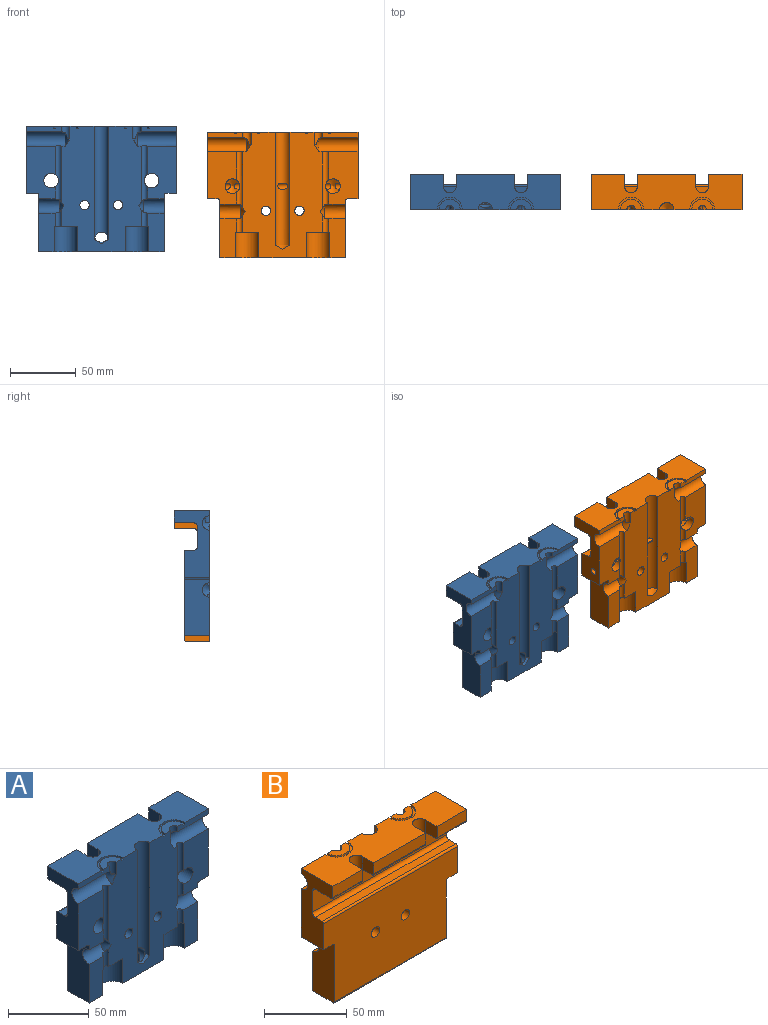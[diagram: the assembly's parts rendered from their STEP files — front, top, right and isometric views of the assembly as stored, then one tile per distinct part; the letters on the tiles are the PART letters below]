
ASSEMBLY  parts=2 mates=1
PART A: 290 faces, bbox 114.3x27x95.3 mm
  f0: plane 114.3x62.55mm, normal (0,1,0), area 5860.2mm2, adj f8,f29,f30,f37,f38,f39,f40,f41
  f1: plane 114.3x15.56mm, normal (0,1,0), area 1721.2mm2, adj f8,f32,f33,f37,f74,f75,f76,f77
  f2: plane 29.36x12.55mm, normal (0,-1,0), area 353.2mm2, adj f5,f21,f43,f60,f61,f73
  f3: plane 39.68x22.07mm, normal (0,-1,0), area 757.8mm2, adj f6,f8,f43,f44,f45,f64,f70,f73
  f4: plane 95.25x60.66mm, normal (0,-1,0), area 4067.1mm2, adj f5,f6,f9,f10,f11,f12,f16,f17
  f5: cylinder r=2.37mm len=12.68mm, axis (0,0,-1), area 83.3mm2, adj f2,f4,f61,f72,f73
  f6: cylinder r=2.37mm len=42.57mm, axis (0,0,-1), area 275.6mm2, adj f3,f4,f64,f70,f72,f73
  f7: plane 26.99x3.96mm, normal (0,-1,0), area 104.9mm2, adj f8,f9,f22,f23,f52,f53,f54,f70
  f8: plane 50.8x26.99mm, normal (1,0,0), area 800.2mm2, adj f0,f1,f3,f7,f22,f25,f30,f31
  f9: cylinder r=3.17mm len=9.53mm, axis (0,0,1), area 66.9mm2, adj f4,f7,f10,f23,f70,f71
  f10: plane 2.91x1.9mm, normal (0,0,1), area 1.4mm2, adj f4,f9,f71
  f11: cylinder r=2.37mm len=12.68mm, axis (0,0,-1), area 83.3mm2, adj f4,f14,f59,f68,f69
  f12: cylinder r=2.37mm len=42.57mm, axis (0,0,-1), area 275.5mm2, adj f4,f13,f65,f66,f68,f69
  f13: plane 39.68x22.07mm, normal (0,-1,0), area 757.8mm2, adj f12,f37,f38,f39,f40,f65,f66,f68
  f14: plane 29.36x12.55mm, normal (0,-1,0), area 353.2mm2, adj f11,f21,f38,f58,f59,f68
  f15: plane 26.99x3.96mm, normal (0,-1,0), area 104.9mm2, adj f16,f22,f28,f37,f55,f56,f57,f66
  f16: cylinder r=3.17mm len=9.53mm, axis (0,0,1), area 66.9mm2, adj f4,f15,f17,f28,f66,f67
  f17: plane 2.91x1.9mm, normal (0,0,1), area 1.4mm2, adj f4,f16,f67
  f18: cylinder r=5.56mm len=85.73mm, axis (0,0,1), area 1450mm2, adj f4,f19,f22,f62,f63
  f19: cone r=0mm half-angle=59deg, axis (0,0,1), area 29mm2, adj f4,f18,f63
  f20: cylinder r=5.08mm len=10.16mm, axis (0,0,-1), area 173.5mm2, adj f21,f62
  f21: plane 95.25x17.78mm, normal (0,0,-1), area 1364.2mm2, adj f2,f4,f14,f20,f29,f38,f43,f58
  f22: plane 114.3x26.99mm, normal (0,0,1), area 2498.3mm2, adj f4,f7,f8,f15,f18,f24,f25,f36
  f23: plane 15.88x7.94mm, normal (0,0,1), area 83.1mm2, adj f4,f7,f9,f53
  f24: plane 44.45x8.26mm, normal (0,1,0), area 366.9mm2, adj f22,f27,f46,f51
  f25: plane 25.4x8.26mm, normal (0,1,0), area 209.7mm2, adj f8,f22,f35,f48
  f26: cylinder r=1.27mm len=25.4mm, axis (-1,0,0), area 50.7mm2, adj f34,f36,f37,f49
  f27: cylinder r=1.27mm len=44.45mm, axis (-1,0,0), area 88.7mm2, adj f24,f34,f46,f51
  f28: plane 15.88x7.94mm, normal (0,0,1), area 83.1mm2, adj f4,f15,f16,f56
  f29: cylinder r=1.27mm len=95.25mm, axis (-1,0,0), area 190mm2, adj f0,f21,f38,f43
  f30: cylinder r=1.27mm len=114.3mm, axis (-1,0,0), area 228mm2, adj f0,f8,f31,f37
  f31: plane 114.3x5.72mm, normal (0,0,1), area 653.2mm2, adj f8,f30,f32,f37
  f32: cylinder r=2.54mm len=114.3mm, axis (-1,0,0), area 456mm2, adj f1,f8,f31,f37
  f33: cylinder r=2.54mm len=114.3mm, axis (-1,0,0), area 456mm2, adj f1,f8,f34,f37
  f34: plane 114.3x13.65mm, normal (0,0,-1), area 1332mm2, adj f8,f26,f27,f33,f35,f37,f46,f47
  f35: cylinder r=1.27mm len=25.4mm, axis (-1,0,0), area 50.7mm2, adj f8,f25,f34,f48
  f36: plane 25.4x8.26mm, normal (0,1,0), area 209.7mm2, adj f22,f26,f37,f49
  f37: plane 50.8x26.99mm, normal (-1,0,0), area 800.2mm2, adj f0,f1,f13,f15,f22,f26,f30,f31
  f38: plane 43.18x19.05mm, normal (-1,0,0), area 773.6mm2, adj f0,f13,f14,f21,f29,f40,f68
  f39: plane 19.05x8.26mm, normal (0,0,-1), area 157.3mm2, adj f0,f13,f37,f40
  f40: cylinder r=1.27mm len=19.05mm, axis (0,-1,0), area 38mm2, adj f0,f13,f38,f39
  f41: cylinder r=3.56mm len=19.05mm, axis (0,-1,0), area 425.6mm2, adj f0,f4
  f42: cylinder r=3.56mm len=19.05mm, axis (0,-1,0), area 425.6mm2, adj f0,f4
  f43: plane 43.18x19.05mm, normal (1,0,0), area 773.6mm2, adj f0,f2,f3,f21,f29,f45,f73
  f44: plane 19.05x8.26mm, normal (0,0,-1), area 157.3mm2, adj f0,f3,f8,f45
  f45: cylinder r=1.27mm len=19.05mm, axis (0,-1,0), area 38mm2, adj f0,f3,f43,f44
  f46: plane 9.53x9.53mm, normal (1,0,0), area 90.4mm2, adj f22,f24,f27,f34,f47
  f47: cylinder r=4.76mm len=9.53mm, axis (0,0,1), area 142.5mm2, adj f22,f34,f46,f48
  f48: plane 9.53x9.53mm, normal (-1,0,0), area 90.4mm2, adj f22,f25,f34,f35,f47
  f49: plane 9.53x9.53mm, normal (1,0,0), area 90.4mm2, adj f22,f26,f34,f36,f50
  f50: cylinder r=4.76mm len=9.53mm, axis (0,0,1), area 142.5mm2, adj f22,f34,f49,f51
  f51: plane 9.53x9.53mm, normal (-1,0,0), area 90.4mm2, adj f22,f24,f27,f34,f50
  f52: cylinder r=9.53mm len=19.05mm, axis (0,0,1), area 38mm2, adj f4,f7,f22,f54
  f53: cylinder r=7.94mm len=15.88mm, axis (0,0,1), area 31.7mm2, adj f4,f7,f23,f54
  f54: plane 19.05x9.53mm, normal (0,0,1), area 43.5mm2, adj f4,f7,f52,f53
  f55: cylinder r=9.53mm len=19.05mm, axis (0,0,1), area 38mm2, adj f4,f15,f22,f57
  f56: cylinder r=7.94mm len=15.88mm, axis (0,0,1), area 31.7mm2, adj f4,f15,f28,f57
  f57: plane 19.05x9.53mm, normal (0,0,1), area 43.5mm2, adj f4,f15,f55,f56
  f58: cylinder r=8.89mm len=19.05mm, axis (0,0,-1), area 532mm2, adj f4,f14,f21,f59
  f59: plane 17.78x8.89mm, normal (0,0,-1), area 115.3mm2, adj f4,f11,f14,f58
  f60: cylinder r=8.89mm len=19.05mm, axis (0,0,-1), area 532mm2, adj f2,f4,f21,f61
  f61: plane 17.78x8.89mm, normal (0,0,-1), area 115.3mm2, adj f2,f4,f5,f60
  f62: cylinder r=5.56mm len=15.24mm, axis (0,1,0), area 427.5mm2, adj f0,f18,f20,f63
  f63: cone r=0mm half-angle=59deg, axis (0,1,0), area 48.4mm2, adj f18,f19,f62
  f64: cylinder r=5.56mm len=19.05mm, axis (0,1,0), area 642.7mm2, adj f0,f3,f6
  f65: cylinder r=5.56mm len=19.05mm, axis (0,1,0), area 642.7mm2, adj f0,f12,f13
  f66: cylinder r=5.56mm len=29.85mm, axis (-1,0,0), area 505.3mm2, adj f4,f12,f13,f15,f16,f37,f67
  f67: cone r=0mm half-angle=59deg, axis (-1,0,0), area 37.8mm2, adj f4,f16,f17,f66
  f68: cylinder r=5.56mm len=15.88mm, axis (-1,0,0), area 263.8mm2, adj f11,f12,f13,f14,f38,f69
  f69: cone r=0mm half-angle=59deg, axis (-1,0,0), area 47.8mm2, adj f4,f11,f12,f68
  f70: cylinder r=5.56mm len=29.85mm, axis (1,0,0), area 505.3mm2, adj f3,f4,f6,f7,f8,f9,f71
  f71: cone r=0mm half-angle=59deg, axis (1,0,0), area 37.8mm2, adj f4,f9,f10,f70
  f72: cone r=0mm half-angle=59deg, axis (1,0,0), area 47.8mm2, adj f4,f5,f6,f73
  f73: cylinder r=5.56mm len=15.88mm, axis (1,0,0), area 263.8mm2, adj f2,f3,f5,f6,f43,f72
  f74: plane 1.27x0.59mm, normal (0,0,1), area 0.7mm2, adj f1,f75,f77,f78
  f75: plane 5.04x1.27mm, normal (1,0,0), area 6.4mm2, adj f1,f74,f76,f78
  f76: plane 1.27x0.59mm, normal (0,0,-1), area 0.7mm2, adj f1,f75,f77,f78
  f77: plane 5.04x1.27mm, normal (-1,0,0), area 6.4mm2, adj f1,f74,f76,f78
  f78: plane 5.04x0.59mm, normal (0,1,0), area 2.9mm2, adj f74,f75,f76,f77
  f79: extruded ~1.9x1.27mm, area 2.6mm2, adj f1,f80,f94,f95
  f80: extruded ~1.7x1.27mm, area 2.4mm2, adj f1,f79,f81,f95
  f81: extruded ~1.72x1.27mm, area 2.4mm2, adj f1,f80,f82,f95
  f82: extruded ~1.91x1.27mm, area 2.6mm2, adj f1,f81,f83,f95
  f83: extruded ~1.92x1.27mm, area 2.6mm2, adj f1,f82,f84,f95
  f84: extruded ~1.72x1.27mm, area 2.4mm2, adj f1,f83,f85,f95
  f85: extruded ~1.7x1.27mm, area 2.4mm2, adj f1,f84,f94,f95
  f86: extruded ~1.54x1.27mm, area 2.1mm2, adj f87,f93,f95,f96
  f87: extruded ~1.27x1.27mm, area 1.8mm2, adj f86,f88,f95,f96
  f88: extruded ~1.27x1.26mm, area 1.8mm2, adj f87,f89,f95,f96
  f89: extruded ~1.54x1.27mm, area 2.1mm2, adj f88,f90,f95,f96
  f90: extruded ~1.55x1.27mm, area 2.1mm2, adj f89,f91,f95,f96
  f91: extruded ~1.27x1.26mm, area 1.8mm2, adj f90,f92,f95,f96
  f92: extruded ~1.27x1.27mm, area 1.8mm2, adj f91,f93,f95,f96
  f93: extruded ~1.55x1.27mm, area 2.1mm2, adj f86,f92,f95,f96
  f94: extruded ~1.9x1.27mm, area 2.6mm2, adj f1,f79,f85,f95
  f95: plane 5.19x4.63mm, normal (0,1,0), area 8mm2, adj f79,f80,f81,f82,f83,f84,f85,f86
  f96: plane 4.15x3.39mm, normal (0,1,0), area 11.7mm2, adj f86,f87,f88,f89,f90,f91,f92,f93
  f97: extruded ~1.27x0.84mm, area 1.2mm2, adj f1,f98,f121,f122
  f98: extruded ~1.27x1.09mm, area 1.6mm2, adj f1,f97,f99,f122
  f99: extruded ~1.27x0.7mm, area 1mm2, adj f1,f98,f100,f122
  f100: extruded ~1.27x0.33mm, area 0.6mm2, adj f1,f99,f101,f122
  f101: extruded ~1.27x0.43mm, area 0.6mm2, adj f1,f100,f102,f122
  f102: extruded ~1.27x0.55mm, area 0.8mm2, adj f1,f101,f103,f122
  f103: extruded ~1.27x0.73mm, area 1mm2, adj f1,f102,f104,f122
  f104: extruded ~1.27x1.21mm, area 1.6mm2, adj f1,f103,f105,f122
  f105: plane 1.27x0.51mm, normal (0.94,0,0.34), area 0.7mm2, adj f1,f104,f106,f122
  f106: extruded ~1.38x1.27mm, area 1.8mm2, adj f1,f105,f107,f122
  f107: extruded ~1.27x1.16mm, area 1.6mm2, adj f1,f106,f108,f122
  f108: extruded ~1.27x0.93mm, area 1.4mm2, adj f1,f107,f109,f122
  f109: extruded ~1.27x0.9mm, area 1.2mm2, adj f1,f108,f110,f122
  f110: extruded ~1.27x1mm, area 1.5mm2, adj f1,f109,f111,f122
  f111: extruded ~1.27x0.75mm, area 1mm2, adj f1,f110,f112,f122
  f112: extruded ~1.27x0.35mm, area 0.6mm2, adj f1,f111,f113,f122
  f113: extruded ~1.27x0.43mm, area 0.6mm2, adj f1,f112,f114,f122
  f114: extruded ~1.27x0.62mm, area 0.9mm2, adj f1,f113,f115,f122
  f115: extruded ~1.27x0.88mm, area 1.2mm2, adj f1,f114,f116,f122
  f116: extruded ~1.27x0.72mm, area 0.9mm2, adj f1,f115,f117,f122
  f117: extruded ~1.27x0.68mm, area 0.9mm2, adj f1,f116,f118,f122
  f118: plane 1.27x0.56mm, normal (-1,0,0), area 0.7mm2, adj f1,f117,f119,f122
  f119: extruded ~1.38x1.27mm, area 1.8mm2, adj f1,f118,f120,f122
  f120: extruded ~1.31x1.27mm, area 1.8mm2, adj f1,f119,f121,f122
  f121: extruded ~1.27x1.04mm, area 1.5mm2, adj f1,f97,f120,f122
  f122: plane 5.18x3.17mm, normal (0,1,0), area 5.9mm2, adj f97,f98,f99,f100,f101,f102,f103,f104
  f123: plane 1.27x0.59mm, normal (0,0,1), area 0.7mm2, adj f1,f124,f126,f127
  f124: plane 5.04x1.27mm, normal (1,0,0), area 6.4mm2, adj f1,f123,f125,f127
  f125: plane 1.27x0.59mm, normal (0,0,-1), area 0.7mm2, adj f1,f124,f126,f127
  f126: plane 5.04x1.27mm, normal (-1,0,0), area 6.4mm2, adj f1,f123,f125,f127
  f127: plane 5.04x0.59mm, normal (0,1,0), area 2.9mm2, adj f123,f124,f125,f126
  f128: extruded ~1.27x0.84mm, area 1.2mm2, adj f1,f129,f152,f153
  f129: extruded ~1.27x1.09mm, area 1.6mm2, adj f1,f128,f130,f153
  f130: extruded ~1.27x0.7mm, area 1mm2, adj f1,f129,f131,f153
  f131: extruded ~1.27x0.33mm, area 0.6mm2, adj f1,f130,f132,f153
  f132: extruded ~1.27x0.43mm, area 0.6mm2, adj f1,f131,f133,f153
  f133: extruded ~1.27x0.55mm, area 0.8mm2, adj f1,f132,f134,f153
  f134: extruded ~1.27x0.73mm, area 1mm2, adj f1,f133,f135,f153
  f135: extruded ~1.27x1.21mm, area 1.6mm2, adj f1,f134,f136,f153
  f136: plane 1.27x0.51mm, normal (0.94,0,0.34), area 0.7mm2, adj f1,f135,f137,f153
  f137: extruded ~1.38x1.27mm, area 1.8mm2, adj f1,f136,f138,f153
  f138: extruded ~1.27x1.16mm, area 1.6mm2, adj f1,f137,f139,f153
  f139: extruded ~1.27x0.93mm, area 1.4mm2, adj f1,f138,f140,f153
  f140: extruded ~1.27x0.9mm, area 1.2mm2, adj f1,f139,f141,f153
  f141: extruded ~1.27x1mm, area 1.5mm2, adj f1,f140,f142,f153
  f142: extruded ~1.27x0.75mm, area 1mm2, adj f1,f141,f143,f153
  f143: extruded ~1.27x0.35mm, area 0.6mm2, adj f1,f142,f144,f153
  f144: extruded ~1.27x0.43mm, area 0.6mm2, adj f1,f143,f145,f153
  f145: extruded ~1.27x0.62mm, area 0.9mm2, adj f1,f144,f146,f153
  f146: extruded ~1.27x0.88mm, area 1.2mm2, adj f1,f145,f147,f153
  f147: extruded ~1.27x0.72mm, area 0.9mm2, adj f1,f146,f148,f153
  f148: extruded ~1.27x0.68mm, area 0.9mm2, adj f1,f147,f149,f153
  f149: plane 1.27x0.56mm, normal (-1,0,0), area 0.7mm2, adj f1,f148,f150,f153
  f150: extruded ~1.38x1.27mm, area 1.8mm2, adj f1,f149,f151,f153
  f151: extruded ~1.31x1.27mm, area 1.8mm2, adj f1,f150,f152,f153
  f152: extruded ~1.27x1.04mm, area 1.5mm2, adj f1,f128,f151,f153
  f153: plane 5.18x3.17mm, normal (0,1,0), area 5.9mm2, adj f128,f129,f130,f131,f132,f133,f134,f135
  f154: extruded ~1.9x1.27mm, area 2.6mm2, adj f1,f155,f169,f170
  f155: extruded ~1.7x1.27mm, area 2.4mm2, adj f1,f154,f156,f170
  f156: extruded ~1.72x1.27mm, area 2.4mm2, adj f1,f155,f157,f170
  f157: extruded ~1.91x1.27mm, area 2.6mm2, adj f1,f156,f158,f170
  f158: extruded ~1.92x1.27mm, area 2.6mm2, adj f1,f157,f159,f170
  f159: extruded ~1.72x1.27mm, area 2.4mm2, adj f1,f158,f160,f170
  f160: extruded ~1.7x1.27mm, area 2.4mm2, adj f1,f159,f169,f170
  f161: extruded ~1.54x1.27mm, area 2.1mm2, adj f162,f168,f170,f171
  f162: extruded ~1.27x1.27mm, area 1.8mm2, adj f161,f163,f170,f171
  f163: extruded ~1.27x1.26mm, area 1.8mm2, adj f162,f164,f170,f171
  f164: extruded ~1.54x1.27mm, area 2.1mm2, adj f163,f165,f170,f171
  f165: extruded ~1.55x1.27mm, area 2.1mm2, adj f164,f166,f170,f171
  f166: extruded ~1.27x1.26mm, area 1.8mm2, adj f165,f167,f170,f171
  f167: extruded ~1.27x1.27mm, area 1.8mm2, adj f166,f168,f170,f171
  f168: extruded ~1.55x1.27mm, area 2.1mm2, adj f161,f167,f170,f171
  f169: extruded ~1.9x1.27mm, area 2.6mm2, adj f1,f154,f160,f170
  f170: plane 5.19x4.63mm, normal (0,1,0), area 8mm2, adj f154,f155,f156,f157,f158,f159,f160,f161
  f171: plane 4.15x3.39mm, normal (0,1,0), area 11.7mm2, adj f161,f162,f163,f164,f165,f166,f167,f168
  f172: extruded ~1.9x1.27mm, area 2.6mm2, adj f0,f173,f191,f192
  f173: extruded ~1.7x1.27mm, area 2.4mm2, adj f0,f172,f174,f192
  f174: extruded ~1.72x1.27mm, area 2.4mm2, adj f0,f173,f175,f192
  f175: extruded ~1.91x1.27mm, area 2.6mm2, adj f0,f174,f176,f192
  f176: extruded ~1.92x1.27mm, area 2.6mm2, adj f0,f175,f177,f192
  f177: extruded ~1.72x1.27mm, area 2.4mm2, adj f0,f176,f178,f192
  f178: plane 1.27x0.19mm, normal (0.04,0,1), area 0.2mm2, adj f0,f177,f179,f192
  f179: plane 1.27x1.14mm, normal (-0.76,0,0.65), area 1.9mm2, adj f0,f178,f180,f192
  f180: plane 1.27x0.85mm, normal (0,0,1), area 1.1mm2, adj f0,f179,f181,f192
  f181: plane 1.27x1.25mm, normal (0.72,0,-0.69), area 2.2mm2, adj f0,f180,f182,f192
  f182: extruded ~1.27x1.1mm, area 1.8mm2, adj f0,f181,f191,f192
  f183: extruded ~1.54x1.27mm, area 2.1mm2, adj f184,f190,f192,f193
  f184: extruded ~1.27x1.27mm, area 1.8mm2, adj f183,f185,f192,f193
  f185: extruded ~1.27x1.26mm, area 1.8mm2, adj f184,f186,f192,f193
  f186: extruded ~1.54x1.27mm, area 2.1mm2, adj f185,f187,f192,f193
  f187: extruded ~1.55x1.27mm, area 2.1mm2, adj f186,f188,f192,f193
  f188: extruded ~1.27x1.26mm, area 1.8mm2, adj f187,f189,f192,f193
  f189: extruded ~1.27x1.27mm, area 1.8mm2, adj f188,f190,f192,f193
  f190: extruded ~1.55x1.27mm, area 2.1mm2, adj f183,f189,f192,f193
  f191: extruded ~1.61x1.27mm, area 2.1mm2, adj f0,f172,f182,f192
  f192: plane 6.32x4.63mm, normal (0,1,0), area 9mm2, adj f172,f173,f174,f175,f176,f177,f178,f179
  f193: plane 4.15x3.39mm, normal (0,1,0), area 11.7mm2, adj f183,f184,f185,f186,f187,f188,f189,f190
  f194: plane 1.27x0.52mm, normal (1,0,0), area 0.7mm2, adj f0,f195,f205,f206
  f195: plane 2.22x1.27mm, normal (0,0,-1), area 2.8mm2, adj f0,f194,f196,f206
  f196: plane 1.85x1.27mm, normal (1,0,0), area 2.4mm2, adj f0,f195,f197,f206
  f197: plane 2.09x1.27mm, normal (0,0,1), area 2.7mm2, adj f0,f196,f198,f206
  f198: plane 1.27x0.52mm, normal (1,0,0), area 0.7mm2, adj f0,f197,f199,f206
  f199: plane 2.09x1.27mm, normal (0,0,-1), area 2.7mm2, adj f0,f198,f200,f206
  f200: plane 1.62x1.27mm, normal (1,0,0), area 2.1mm2, adj f0,f199,f201,f206
  f201: plane 2.22x1.27mm, normal (0,0,1), area 2.8mm2, adj f0,f200,f202,f206
  f202: plane 1.27x0.52mm, normal (1,0,0), area 0.7mm2, adj f0,f201,f203,f206
  f203: plane 2.81x1.27mm, normal (0,0,-1), area 3.6mm2, adj f0,f202,f204,f206
  f204: plane 5.04x1.27mm, normal (-1,0,0), area 6.4mm2, adj f0,f203,f205,f206
  f205: plane 2.81x1.27mm, normal (0,0,1), area 3.6mm2, adj f0,f194,f204,f206
  f206: plane 5.04x2.81mm, normal (0,1,0), area 6.3mm2, adj f194,f195,f196,f197,f198,f199,f200,f201
  f207: plane 1.27x0.52mm, normal (1,0,0), area 0.7mm2, adj f0,f208,f218,f219
  f208: plane 2.22x1.27mm, normal (0,0,-1), area 2.8mm2, adj f0,f207,f209,f219
  f209: plane 1.85x1.27mm, normal (1,0,0), area 2.4mm2, adj f0,f208,f210,f219
  f210: plane 2.09x1.27mm, normal (0,0,1), area 2.7mm2, adj f0,f209,f211,f219
  f211: plane 1.27x0.52mm, normal (1,0,0), area 0.7mm2, adj f0,f210,f212,f219
  f212: plane 2.09x1.27mm, normal (0,0,-1), area 2.7mm2, adj f0,f211,f213,f219
  f213: plane 1.62x1.27mm, normal (1,0,0), area 2.1mm2, adj f0,f212,f214,f219
  f214: plane 2.22x1.27mm, normal (0,0,1), area 2.8mm2, adj f0,f213,f215,f219
  f215: plane 1.27x0.52mm, normal (1,0,0), area 0.7mm2, adj f0,f214,f216,f219
  f216: plane 2.81x1.27mm, normal (0,0,-1), area 3.6mm2, adj f0,f215,f217,f219
  f217: plane 5.04x1.27mm, normal (-1,0,0), area 6.4mm2, adj f0,f216,f218,f219
  f218: plane 2.81x1.27mm, normal (0,0,1), area 3.6mm2, adj f0,f207,f217,f219
  f219: plane 5.04x2.81mm, normal (0,1,0), area 6.3mm2, adj f207,f208,f209,f210,f211,f212,f213,f214
  f220: plane 4.15x1.27mm, normal (1,0,0), area 5.3mm2, adj f0,f221,f227,f228
  f221: plane 1.37x1.27mm, normal (0,0,1), area 1.7mm2, adj f0,f220,f222,f228
  f222: plane 1.27x0.89mm, normal (1,0,0), area 1.1mm2, adj f0,f221,f223,f228
  f223: plane 3.8x1.27mm, normal (0,0,-1), area 4.8mm2, adj f0,f222,f224,f228
  f224: plane 1.27x0.89mm, normal (-1,0,0), area 1.1mm2, adj f0,f223,f225,f228
  f225: plane 1.37x1.27mm, normal (0,0,1), area 1.7mm2, adj f0,f224,f226,f228
  f226: plane 4.15x1.27mm, normal (-1,0,0), area 5.3mm2, adj f0,f225,f227,f228
  f227: plane 1.27x1.07mm, normal (0,0,1), area 1.4mm2, adj f0,f220,f226,f228
  f228: plane 5.04x3.8mm, normal (0,1,0), area 7.8mm2, adj f220,f221,f222,f223,f224,f225,f226,f227
  f229: extruded ~1.9x1.27mm, area 2.6mm2, adj f0,f230,f248,f249
  f230: extruded ~1.7x1.27mm, area 2.4mm2, adj f0,f229,f231,f249
  f231: extruded ~1.72x1.27mm, area 2.4mm2, adj f0,f230,f232,f249
  f232: extruded ~1.91x1.27mm, area 2.6mm2, adj f0,f231,f233,f249
  f233: extruded ~1.92x1.27mm, area 2.6mm2, adj f0,f232,f234,f249
  f234: extruded ~1.72x1.27mm, area 2.4mm2, adj f0,f233,f235,f249
  f235: plane 1.27x0.19mm, normal (0.04,0,1), area 0.2mm2, adj f0,f234,f236,f249
  f236: plane 1.27x1.14mm, normal (-0.76,0,0.65), area 1.9mm2, adj f0,f235,f237,f249
  f237: plane 1.27x0.85mm, normal (0,0,1), area 1.1mm2, adj f0,f236,f238,f249
  f238: plane 1.27x1.25mm, normal (0.72,0,-0.69), area 2.2mm2, adj f0,f237,f239,f249
  f239: extruded ~1.27x1.1mm, area 1.8mm2, adj f0,f238,f248,f249
  f240: extruded ~1.54x1.27mm, area 2.1mm2, adj f241,f247,f249,f250
  f241: extruded ~1.27x1.27mm, area 1.8mm2, adj f240,f242,f249,f250
  f242: extruded ~1.27x1.26mm, area 1.8mm2, adj f241,f243,f249,f250
  f243: extruded ~1.54x1.27mm, area 2.1mm2, adj f242,f244,f249,f250
  f244: extruded ~1.55x1.27mm, area 2.1mm2, adj f243,f245,f249,f250
  f245: extruded ~1.27x1.26mm, area 1.8mm2, adj f244,f246,f249,f250
  f246: extruded ~1.27x1.27mm, area 1.8mm2, adj f245,f247,f249,f250
  f247: extruded ~1.55x1.27mm, area 2.1mm2, adj f240,f246,f249,f250
  f248: extruded ~1.61x1.27mm, area 2.1mm2, adj f0,f229,f239,f249
  f249: plane 6.32x4.63mm, normal (0,1,0), area 9mm2, adj f229,f230,f231,f232,f233,f234,f235,f236
  f250: plane 4.15x3.39mm, normal (0,1,0), area 11.7mm2, adj f240,f241,f242,f243,f244,f245,f246,f247
  f251: plane 3x1.27mm, normal (-0.95,0,-0.3), area 4mm2, adj f0,f252,f260,f261
  f252: extruded ~1.27x1.11mm, area 1.4mm2, adj f0,f251,f253,f261
  f253: extruded ~1.27x0.49mm, area 0.6mm2, adj f0,f252,f254,f261
  f254: extruded ~1.27x0.62mm, area 0.8mm2, adj f0,f253,f255,f261
  f255: plane 3x1.27mm, normal (0.95,0,-0.3), area 4mm2, adj f0,f254,f256,f261
  f256: plane 1.27x1.08mm, normal (0,0,-1), area 1.4mm2, adj f0,f255,f257,f261
  f257: plane 5.04x1.71mm, normal (-0.95,0,0.32), area 6.8mm2, adj f0,f256,f258,f261
  f258: plane 1.27x1.16mm, normal (0,0,1), area 1.5mm2, adj f0,f257,f259,f261
  f259: plane 5.04x1.71mm, normal (0.95,0,0.32), area 6.8mm2, adj f0,f258,f260,f261
  f260: plane 1.27x1.08mm, normal (0,0,-1), area 1.4mm2, adj f0,f251,f259,f261
  f261: plane 5.04x4.59mm, normal (0,1,0), area 9.8mm2, adj f251,f252,f253,f254,f255,f256,f257,f258
  f262: plane 1.27x0.88mm, normal (1,0,0), area 1.1mm2, adj f0,f263,f273,f274
  f263: plane 1.83x1.27mm, normal (0,0,-1), area 2.3mm2, adj f0,f262,f264,f274
  f264: plane 1.3x1.27mm, normal (1,0,0), area 1.6mm2, adj f0,f263,f265,f274
  f265: plane 1.71x1.27mm, normal (0,0,1), area 2.2mm2, adj f0,f264,f266,f274
  f266: plane 1.27x0.88mm, normal (1,0,0), area 1.1mm2, adj f0,f265,f267,f274
  f267: plane 1.71x1.27mm, normal (0,0,-1), area 2.2mm2, adj f0,f266,f268,f274
  f268: plane 1.27x1.11mm, normal (1,0,0), area 1.4mm2, adj f0,f267,f269,f274
  f269: plane 1.83x1.27mm, normal (0,0,1), area 2.3mm2, adj f0,f268,f270,f274
  f270: plane 1.27x0.88mm, normal (1,0,0), area 1.1mm2, adj f0,f269,f271,f274
  f271: plane 2.9x1.27mm, normal (0,0,-1), area 3.7mm2, adj f0,f270,f272,f274
  f272: plane 5.04x1.27mm, normal (-1,0,0), area 6.4mm2, adj f0,f271,f273,f274
  f273: plane 2.9x1.27mm, normal (0,0,1), area 3.7mm2, adj f0,f262,f272,f274
  f274: plane 5.04x2.9mm, normal (0,1,0), area 10.1mm2, adj f262,f263,f264,f265,f266,f267,f268,f269
  f275: plane 5.04x1.27mm, normal (1,0,0), area 6.4mm2, adj f0,f276,f288,f289
  f276: plane 1.27x0.96mm, normal (0,0,-1), area 1.2mm2, adj f0,f275,f277,f289
  f277: plane 2.38x1.27mm, normal (-1,0,0), area 3mm2, adj f0,f276,f278,f289
  f278: extruded ~1.39x1.27mm, area 1.8mm2, adj f0,f277,f279,f289
  f279: plane 1.27x0.02mm, normal (0,0,-1), area 0mm2, adj f0,f278,f280,f289
  f280: plane 3.77x2.19mm, normal (0.87,0,-0.5), area 5.5mm2, adj f0,f279,f281,f289
  f281: plane 1.35x1.27mm, normal (0,0,-1), area 1.7mm2, adj f0,f280,f282,f289
  f282: plane 5.04x1.27mm, normal (-1,0,0), area 6.4mm2, adj f0,f281,f283,f289
  f283: plane 1.27x0.95mm, normal (0,0,1), area 1.2mm2, adj f0,f282,f284,f289
  f284: plane 2.37x1.27mm, normal (1,0,0), area 3mm2, adj f0,f283,f285,f289
  f285: extruded ~1.44x1.27mm, area 1.8mm2, adj f0,f284,f286,f289
  f286: plane 1.27x0.03mm, normal (0,0,1), area 0mm2, adj f0,f285,f287,f289
  f287: plane 3.81x2.19mm, normal (-0.87,0,0.5), area 5.6mm2, adj f0,f286,f288,f289
  f288: plane 1.36x1.27mm, normal (0,0,1), area 1.7mm2, adj f0,f275,f287,f289
  f289: plane 5.04x4.47mm, normal (0,1,0), area 14.4mm2, adj f275,f276,f277,f278,f279,f280,f281,f282
PART B: 77 faces, bbox 114.3x27x95.3 mm
  f0: cylinder r=5.56mm len=85.73mm, axis (0,0,1), area 1466.2mm2, adj f7,f24,f60,f75
  f1: cylinder r=5.56mm len=11.13mm, axis (0,1,0), area 180.7mm2, adj f2,f6,f8,f75,f76
  f2: cone r=0mm half-angle=59deg, axis (0,1,0), area 77.1mm2, adj f1,f75,f76
  f3: cylinder r=5.56mm len=11.13mm, axis (0,1,0), area 180.7mm2, adj f4,f14,f16,f74,f75
  f4: cone r=0mm half-angle=59deg, axis (0,1,0), area 77.1mm2, adj f3,f74,f75
  f5: plane 29.36x12.55mm, normal (0,1,0), area 353.2mm2, adj f9,f21,f45,f63,f64,f72
  f6: plane 39.68x22.07mm, normal (0,1,0), area 757.8mm2, adj f1,f8,f11,f45,f46,f47,f69,f72
  f7: plane 95.25x60.66mm, normal (0,1,0), area 4067.1mm2, adj f0,f8,f9,f12,f13,f14,f15,f19
  f8: cylinder r=2.37mm len=42.57mm, axis (0,0,-1), area 275.5mm2, adj f1,f6,f7,f69,f71,f72
  f9: cylinder r=2.37mm len=12.68mm, axis (0,0,-1), area 83.3mm2, adj f5,f7,f63,f71,f72
  f10: plane 26.99x3.96mm, normal (0,1,0), area 104.9mm2, adj f11,f13,f23,f24,f54,f55,f56,f69
  f11: plane 50.8x26.99mm, normal (1,0,0), area 782.5mm2, adj f6,f10,f24,f26,f28,f29,f31,f34
  f12: plane 2.91x1.9mm, normal (0,0,1), area 1.4mm2, adj f7,f13,f70
  f13: cylinder r=3.17mm len=9.53mm, axis (0,0,1), area 66.7mm2, adj f7,f10,f12,f23,f69,f70
  f14: cylinder r=2.37mm len=42.57mm, axis (0,0,-1), area 275.6mm2, adj f3,f7,f16,f65,f67,f68
  f15: cylinder r=2.37mm len=12.68mm, axis (0,0,-1), area 83.3mm2, adj f7,f17,f61,f67,f68
  f16: plane 39.68x22.07mm, normal (0,1,0), area 757.8mm2, adj f3,f14,f39,f40,f41,f42,f65,f67
  f17: plane 29.36x12.55mm, normal (0,1,0), area 353.2mm2, adj f15,f21,f40,f61,f62,f67
  f18: plane 26.99x3.96mm, normal (0,1,0), area 104.9mm2, adj f19,f22,f24,f39,f57,f58,f59,f65
  f19: cylinder r=3.17mm len=9.53mm, axis (0,0,1), area 66.7mm2, adj f7,f18,f20,f22,f65,f66
  f20: plane 2.91x1.9mm, normal (0,0,1), area 1.4mm2, adj f7,f19,f66
  f21: plane 95.25x17.78mm, normal (0,0,-1), area 1445.3mm2, adj f5,f7,f17,f30,f40,f45,f62,f64
  f22: plane 15.88x7.94mm, normal (0,0,1), area 83.1mm2, adj f7,f18,f19,f58
  f23: plane 15.88x7.94mm, normal (0,0,1), area 83.1mm2, adj f7,f10,f13,f55
  f24: plane 114.3x26.99mm, normal (0,0,1), area 2498.3mm2, adj f0,f7,f10,f11,f18,f25,f26,f32
  f25: plane 44.45x8.26mm, normal (0,-1,0), area 366.9mm2, adj f24,f27,f50,f52
  f26: plane 25.4x8.26mm, normal (0,-1,0), area 209.7mm2, adj f11,f24,f28,f48
  f27: cylinder r=1.27mm len=44.45mm, axis (-1,0,0), area 88.7mm2, adj f25,f29,f50,f52
  f28: cylinder r=1.27mm len=25.4mm, axis (-1,0,0), area 50.7mm2, adj f11,f26,f29,f48
  f29: plane 114.3x13.65mm, normal (0,0,-1), area 1332mm2, adj f11,f27,f28,f33,f34,f39,f48,f49
  f30: cylinder r=1.27mm len=95.25mm, axis (-1,0,0), area 190mm2, adj f21,f31,f40,f45
  f31: plane 114.3x62.55mm, normal (0,-1,0), area 6247.8mm2, adj f11,f30,f38,f39,f40,f41,f42,f43
  f32: plane 25.4x8.26mm, normal (0,-1,0), area 209.7mm2, adj f24,f33,f39,f53
  f33: cylinder r=1.27mm len=25.4mm, axis (-1,0,0), area 50.7mm2, adj f29,f32,f39,f53
  f34: cylinder r=2.54mm len=114.3mm, axis (-1,0,0), area 456mm2, adj f11,f29,f35,f39
  f35: plane 114.3x15.56mm, normal (0,-1,0), area 1778.2mm2, adj f11,f34,f36,f39
  f36: cylinder r=2.54mm len=114.3mm, axis (-1,0,0), area 456mm2, adj f11,f35,f37,f39
  f37: plane 114.3x5.72mm, normal (0,0,1), area 653.2mm2, adj f11,f36,f38,f39
  f38: cylinder r=1.27mm len=114.3mm, axis (-1,0,0), area 228mm2, adj f11,f31,f37,f39
  f39: plane 50.8x26.99mm, normal (-1,0,0), area 800.2mm2, adj f16,f18,f24,f29,f31,f32,f33,f34
  f40: plane 43.18x19.05mm, normal (-1,0,0), area 773.6mm2, adj f16,f17,f21,f30,f31,f41,f67
  f41: cylinder r=1.27mm len=19.05mm, axis (0,-1,0), area 38mm2, adj f16,f31,f40,f42
  f42: plane 19.05x8.26mm, normal (0,0,-1), area 157.3mm2, adj f16,f31,f39,f41
  f43: cylinder r=3.56mm len=19.05mm, axis (0,-1,0), area 425.6mm2, adj f7,f31
  f44: cylinder r=3.56mm len=19.05mm, axis (0,-1,0), area 425.6mm2, adj f7,f31
  f45: plane 43.18x19.05mm, normal (1,0,0), area 773.6mm2, adj f5,f6,f21,f30,f31,f46,f72
  f46: cylinder r=1.27mm len=19.05mm, axis (0,-1,0), area 38mm2, adj f6,f31,f45,f47
  f47: plane 19.05x8.26mm, normal (0,0,-1), area 157.3mm2, adj f6,f11,f31,f46
  f48: plane 9.53x9.53mm, normal (-1,0,0), area 90.4mm2, adj f24,f26,f28,f29,f49
  f49: cylinder r=4.76mm len=9.53mm, axis (0,0,1), area 142.5mm2, adj f24,f29,f48,f50
  f50: plane 9.53x9.53mm, normal (1,0,0), area 90.4mm2, adj f24,f25,f27,f29,f49
  f51: cylinder r=4.76mm len=9.53mm, axis (0,0,1), area 142.5mm2, adj f24,f29,f52,f53
  f52: plane 9.53x9.53mm, normal (-1,0,0), area 90.4mm2, adj f24,f25,f27,f29,f51
  f53: plane 9.53x9.53mm, normal (1,0,0), area 90.4mm2, adj f24,f29,f32,f33,f51
  f54: cylinder r=9.53mm len=19.05mm, axis (0,0,1), area 38mm2, adj f7,f10,f24,f56
  f55: cylinder r=7.94mm len=15.88mm, axis (0,0,1), area 31.7mm2, adj f7,f10,f23,f56
  f56: plane 19.05x9.53mm, normal (0,0,1), area 43.5mm2, adj f7,f10,f54,f55
  f57: cylinder r=9.53mm len=19.05mm, axis (0,0,1), area 38mm2, adj f7,f18,f24,f59
  f58: cylinder r=7.94mm len=15.88mm, axis (0,0,1), area 31.7mm2, adj f7,f18,f22,f59
  f59: plane 19.05x9.53mm, normal (0,0,1), area 43.5mm2, adj f7,f18,f57,f58
  f60: cone r=0mm half-angle=59deg, axis (0,0,1), area 56.7mm2, adj f0,f7
  f61: plane 17.78x8.89mm, normal (0,0,-1), area 115.3mm2, adj f7,f15,f17,f62
  f62: cylinder r=8.89mm len=19.05mm, axis (0,0,-1), area 532mm2, adj f7,f17,f21,f61
  f63: plane 17.78x8.89mm, normal (0,0,-1), area 115.3mm2, adj f5,f7,f9,f64
  f64: cylinder r=8.89mm len=19.05mm, axis (0,0,-1), area 532mm2, adj f5,f7,f21,f63
  f65: cylinder r=5.56mm len=29.85mm, axis (-1,0,0), area 505.3mm2, adj f7,f14,f16,f18,f19,f39,f66
  f66: cone r=0mm half-angle=59deg, axis (-1,0,0), area 37.8mm2, adj f7,f19,f20,f65
  f67: cylinder r=5.56mm len=15.88mm, axis (-1,0,0), area 263.8mm2, adj f14,f15,f16,f17,f40,f68
  f68: cone r=0mm half-angle=59deg, axis (-1,0,0), area 47.8mm2, adj f7,f14,f15,f67
  f69: cylinder r=5.56mm len=29.85mm, axis (1,0,0), area 505.3mm2, adj f6,f7,f8,f10,f11,f13,f70
  f70: cone r=0mm half-angle=59deg, axis (1,0,0), area 37.8mm2, adj f7,f12,f13,f69
  f71: cone r=0mm half-angle=59deg, axis (1,0,0), area 47.8mm2, adj f7,f8,f9,f72
  f72: cylinder r=5.56mm len=15.88mm, axis (1,0,0), area 263.8mm2, adj f5,f6,f8,f9,f45,f71
  f73: cone r=0mm half-angle=59deg, axis (1,0,0), area 20.7mm2, adj f74
  f74: cylinder r=2.37mm len=4.75mm, axis (1,0,0), area 35.7mm2, adj f3,f4,f73
  f75: cylinder r=2.37mm len=72.98mm, axis (1,0,0), area 983mm2, adj f0,f1,f2,f3,f4
  f76: cylinder r=2.37mm len=17.44mm, axis (1,0,0), area 225.2mm2, adj f1,f2,f11
PLACE A t=(-137.5,-49.69,4.25)mm
PLACE B rot(axis=(0,0,1),180deg) t=(0,-49.69,0)mm fixed
MATE planar B.f7 <-> A.f4  axis (0,-1,0) through (0,-49.69,-45.74)mm
